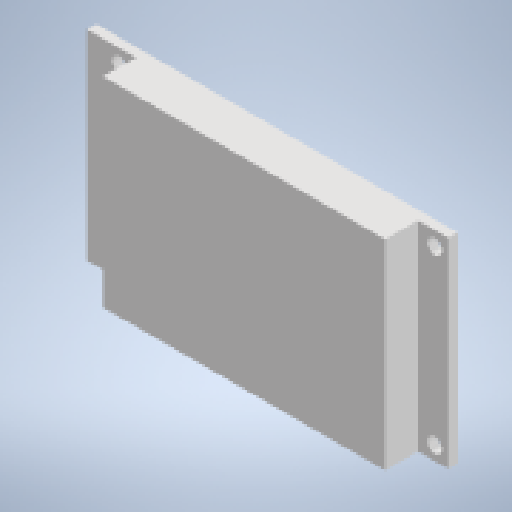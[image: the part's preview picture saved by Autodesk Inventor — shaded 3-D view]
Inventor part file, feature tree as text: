
AUTODESK INVENTOR PART (.ipt)
format: ipt  version: 2023 (Build 270158000, 158)  size: 221,184 bytes
history: native  units: in
note: dims shown in document units (in); Inventor stores cm internally (conversion verified against a paired STEP export)
features: extrude x2, other x1, sketch x1
ambient origin geometry x8: Origin, YZ Plane, XZ Plane, XY Plane, X Axis, Y Axis, Z Axis, Center Point
bodies: Solid1 (feature_tree)
feature tree (4):
  other  "Ecran"
  extrude  "Extrusion1"  Depth=0.2756in
  extrude  "Extrusion2"  Depth=0.2756in
  sketch  "Sketch3"  dims[d2=0.1181in d3=0.126in d4=0.1181in d5=3.0386in d6=0.8409in d8=2.648in d9=0.1181in d10=0.3543in d11=0.0in d12=2.3724in d13=0.2563in d14=0.2563in d15=2.3724in d16=0.2756in d17=0.0in]
